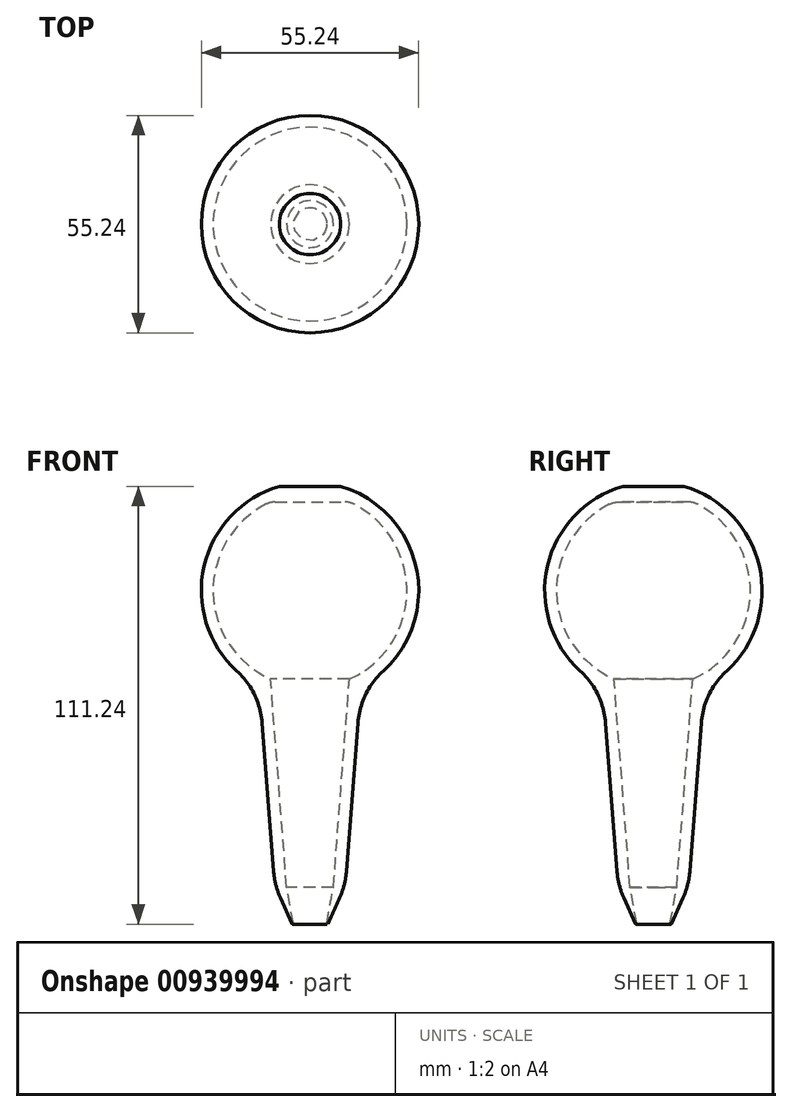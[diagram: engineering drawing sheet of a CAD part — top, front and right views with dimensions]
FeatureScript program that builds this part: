
annotation { "Feature Type Name" : "Feature", "Feature Type Description" : "" }
export const myFeature = defineFeature(function(context is Context, id is Id, definition is map)
    precondition{}
    {
        {
            var Q0;
            Q0=qCreatedBy(makeId("Front.planeOp"),FACE);
            var sketch = newSketch(context, id + "F0", { "sketchPlane" : qUnion([Q0])});
            skPoint(sketch, "E0", {"position": v(0, 65.4) * mm});
            skPoint(sketch, "E1", {"position": v(0, -42.87) * mm});
            skPoint(sketch, "E2", {"position": v(0, 20.4) * mm});
            skLineSegment(sketch, "E3", {"start": v(10, 20.4) * mm, "end": v(5.93, -32.47) * mm});
            skPoint(sketch, "E4", {"position": v(5.38, -39.7) * mm});
            skPoint(sketch, "E5.orphan", {"position": v(5.07, -43.7) * mm});
            skPoint(sketch, "E6.orphan", {"position": v(-10, 20.4) * mm});
            skPoint(sketch, "E7.orphan", {"position": v(-25, 65.4) * mm});
            skArc(sketch, "E8", {"start": v(10, 20.4) * mm, "mid": v(24.62, 42.9) * mm, "end": v(10, 65.4) * mm});
            skArc(sketch, "E9.0", {"start": v(12.86, 18.45) * mm, "mid": v(27.49, 45.63) * mm, "end": v(7.8, 69.4) * mm});
            skLineSegment(sketch, "E9.1", {"start": v(12.86, 18.45) * mm, "end": v(8.98, -32) * mm});
            skPoint(sketch, "E10", {"position": v(10, 65.4) * mm});
            skLineSegment(sketch, "E11.trimOffspring", {"start": v(10, 65.4) * mm, "end": v(0, 65.4) * mm});
            skPoint(sketch, "E12.start.orphan", {"position": v(25, 65.4) * mm});
            skLineSegment(sketch, "E13.0", {"start": v(7.8, 69.4) * mm, "end": v(0, 69.4) * mm});
            skLineSegment(sketch, "E14", {"start": v(0, 69.4) * mm, "end": v(0, 65.4) * mm});
            skPoint(sketch, "E15", {"position": v(8.39, -39.7) * mm});
            skLineSegment(sketch, "E16", {"start": v(4.01, -42.87) * mm, "end": v(5.93, -32.47) * mm});
            skLineSegment(sketch, "E17", {"start": v(4.01, -42.87) * mm, "end": v(8.98, -32) * mm});
            skSolve(sketch);
        }
        {
            var Q0;
            Q0=makeQuery(id+"F0.imprint","IMPRINT",FACE,{"disambiguationData":[TD([[makeQuery(id+"F0.imprint","IMPRINT",EDGE,{"derivedFrom":sQuery(id+"F0.wireOp",EDGE,"E3")}),1.0]])]});
            var Q1;
            Q1=sQuery(id+"F0.wireOp",EDGE,"E14");
            revolve(context, id + "F1", {"surfaceOperationType" : NewSurfaceOperationType.NEW, "entities" : qUnion([Q0]), "axis" : qUnion([Q1]), "revolveType" : RevolveType.FULL});
        }
        {
            var Q0;
            Q0=makeQuery(id+"F1.opRevolve","SWEPT_EDGE",EDGE,{"disambiguationData":[OSD([sQuery(id+"F0.wireOp",EDGE,"E16"),sQuery(id+"F0.wireOp",EDGE,"E17")])]});
            fillet(context, id + "F2", {"entities" : qUnion([Q0]), "radius" : .15 * mm, "tangentPropagation" : true, "allowEdgeOverflow" : false});
        }
        {
            var Q0;
            Q0=makeQuery(id+"F1.opRevolve","SWEPT_EDGE",EDGE,{"disambiguationData":[OSD([sQuery(id+"F0.wireOp",EDGE,"E9.1"),sQuery(id+"F0.wireOp",EDGE,"E17")])]});
            var Q1;
            Q1=makeQuery(id+"F1.opRevolve","SWEPT_EDGE",EDGE,{"disambiguationData":[OSD([sQuery(id+"F0.wireOp",EDGE,"E9.0"),sQuery(id+"F0.wireOp",EDGE,"E9.1")])]});
            fillet(context, id + "F3", {"entities" : qUnion([Q0, Q1]), "radius" : 20 * mm, "tangentPropagation" : true, "allowEdgeOverflow" : false});
        }
        {
            var Q0;
            Q0=makeQuery(id+"F1.opRevolve","SWEPT_EDGE",EDGE,{"disambiguationData":[OSD([sQuery(id+"F0.wireOp",EDGE,"E8"),sQuery(id+"F0.wireOp",EDGE,"E11.trimOffspring")])]});
            fillet(context, id + "F4", {"entities" : qUnion([Q0]), "radius" : 5 * mm, "tangentPropagation" : true, "allowEdgeOverflow" : false});
        }
    });
